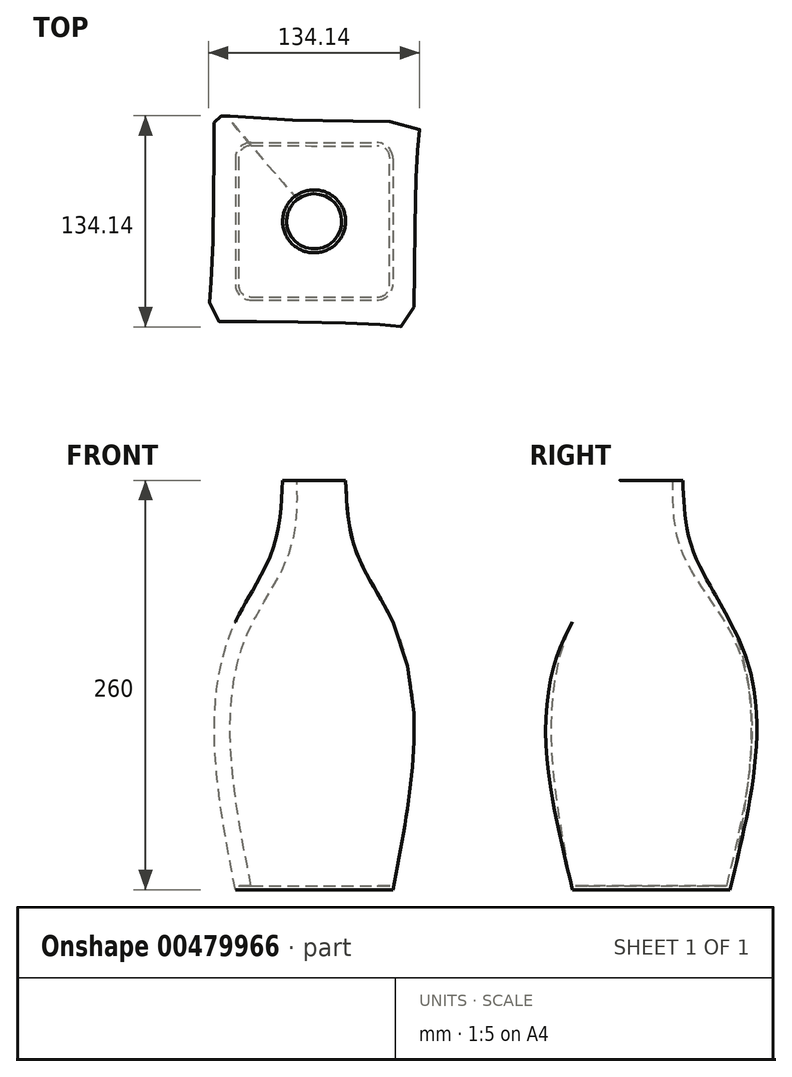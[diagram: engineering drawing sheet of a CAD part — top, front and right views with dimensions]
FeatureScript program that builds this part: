
annotation { "Feature Type Name" : "Feature", "Feature Type Description" : "" }
export const myFeature = defineFeature(function(context is Context, id is Id, definition is map)
    precondition{}
    {
        {
            var Q0;
            Q0=qCreatedBy(makeId("Top.planeOp"),FACE);
            var sketch = newSketch(context, id + "F0", { "sketchPlane" : qUnion([Q0])});
            skLineSegment(sketch, "E0.bottom", {"start": v(10, 0) * mm, "end": v(90, 0) * mm});
            skLineSegment(sketch, "E0.top", {"start": v(10, -100) * mm, "end": v(90, -100) * mm});
            skLineSegment(sketch, "E0.left", {"start": v(0, -10) * mm, "end": v(0, -90) * mm});
            skLineSegment(sketch, "E0.right", {"start": v(100, -10) * mm, "end": v(100, -90) * mm});
            skPoint(sketch, "E1.visualSharp", {"position": v(0, 0) * mm});
            skArc(sketch, "E1.filletArc", {"start": v(10, 0) * mm, "mid": v(2.93, -2.93) * mm, "end": v(0, -10) * mm});
            skPoint(sketch, "E2.visualSharp", {"position": v(100, 0) * mm});
            skArc(sketch, "E2.filletArc", {"start": v(100, -10) * mm, "mid": v(97.07, -2.93) * mm, "end": v(90, 0) * mm});
            skPoint(sketch, "E3.visualSharp", {"position": v(100, -100) * mm});
            skArc(sketch, "E3.filletArc", {"start": v(90, -100) * mm, "mid": v(97.07, -97.07) * mm, "end": v(100, -90) * mm});
            skPoint(sketch, "E4.visualSharp", {"position": v(0, -100) * mm});
            skArc(sketch, "E4.filletArc", {"start": v(0, -90) * mm, "mid": v(2.93, -97.07) * mm, "end": v(10, -100) * mm});
            skSolve(sketch);
        }
        {
            var Q0;
            Q0=qCreatedBy(makeId("Top.planeOp"),FACE);
            cPlane(context, id + "F1", {"entities" : qUnion([Q0]), "cplaneType" : CPlaneType.OFFSET, "offset" : 170 * mm, "width" : 150 * mm, "height" : 150 * mm});
        }
        {
            var Q0;
            Q0=qCreatedBy(id+"F1.planeOp",FACE);
            cPlane(context, id + "F2", {"entities" : qUnion([Q0]), "cplaneType" : CPlaneType.OFFSET, "offset" : 50 * mm, "width" : 150 * mm, "height" : 150 * mm});
        }
        {
            var Q0;
            Q0=qCreatedBy(id+"F2.planeOp",FACE);
            cPlane(context, id + "F3", {"entities" : qUnion([Q0]), "cplaneType" : CPlaneType.OFFSET, "offset" : 40 * mm, "width" : 150 * mm, "height" : 150 * mm});
        }
        {
            var Q0;
            Q0=qCreatedBy(id+"F1.planeOp",FACE);
            var sketch = newSketch(context, id + "F4", { "sketchPlane" : qUnion([Q0])});
            skLineSegment(sketch, "E5.bottom", {"start": v(10, 0) * mm, "end": v(90, 0) * mm});
            skLineSegment(sketch, "E5.top", {"start": v(10, -100) * mm, "end": v(90, -100) * mm});
            skLineSegment(sketch, "E5.left", {"start": v(0, -10) * mm, "end": v(0, -90) * mm});
            skLineSegment(sketch, "E5.right", {"start": v(100, -10) * mm, "end": v(100, -90) * mm});
            skPoint(sketch, "E6.visualSharp", {"position": v(100, 0) * mm});
            skArc(sketch, "E6.filletArc", {"start": v(100, -10) * mm, "mid": v(97.07, -2.93) * mm, "end": v(90, 0) * mm});
            skPoint(sketch, "E7.visualSharp", {"position": v(0, 0) * mm});
            skArc(sketch, "E7.filletArc", {"start": v(10, 0) * mm, "mid": v(2.93, -2.93) * mm, "end": v(0, -10) * mm});
            skPoint(sketch, "E8.visualSharp", {"position": v(0, -100) * mm});
            skArc(sketch, "E8.filletArc", {"start": v(0, -90) * mm, "mid": v(2.93, -97.07) * mm, "end": v(10, -100) * mm});
            skPoint(sketch, "E9.visualSharp", {"position": v(100, -100) * mm});
            skArc(sketch, "E9.filletArc", {"start": v(90, -100) * mm, "mid": v(97.07, -97.07) * mm, "end": v(100, -90) * mm});
            skSolve(sketch);
        }
        {
            var Q0;
            Q0=qCreatedBy(id+"F2.planeOp",FACE);
            var sketch = newSketch(context, id + "F5", { "sketchPlane" : qUnion([Q0])});
            skCircle(sketch, "E10", {"center": v(50, -50) * mm, "radius": 25 * mm});
            skPoint(sketch, "E10.centerSnap0", {"position": v(0, -50) * mm});
            skPoint(sketch, "E10.centerSnap1", {"position": v(50, 0) * mm});
            skSolve(sketch);
        }
        {
            var Q0;
            Q0=qCreatedBy(id+"F3.planeOp",FACE);
            var sketch = newSketch(context, id + "F6", { "sketchPlane" : qUnion([Q0])});
            skCircle(sketch, "E11", {"center": v(50, -50) * mm, "radius": 20 * mm});
            skPoint(sketch, "E11.centerSnap0", {"position": v(50, 0) * mm});
            skPoint(sketch, "E11.centerSnap1", {"position": v(0, -50) * mm});
            skSolve(sketch);
        }
        {
            var Q0;
            Q0=makeQuery(id+"F0.imprint","IMPRINT",FACE,{"disambiguationData":[TD([[makeQuery(id+"F0.imprint","IMPRINT",EDGE,{"derivedFrom":sQuery(id+"F0.wireOp",EDGE,"E0.bottom")}),-1.0]])]});
            var Q1;
            Q1=makeQuery(id+"F4.imprint","IMPRINT",FACE,{"disambiguationData":[TD([[makeQuery(id+"F4.imprint","IMPRINT",EDGE,{"derivedFrom":sQuery(id+"F4.wireOp",EDGE,"E5.bottom")}),-1.0]])]});
            var Q2;
            Q2=makeQuery(id+"F5.imprint","IMPRINT",FACE,{"disambiguationData":[TD([[makeQuery(id+"F5.imprint","IMPRINT",EDGE,{"derivedFrom":sQuery(id+"F5.wireOp",EDGE,"E10")}),1.0]])]});
            var Q3;
            Q3=makeQuery(id+"F6.imprint","IMPRINT",FACE,{"disambiguationData":[TD([[makeQuery(id+"F6.imprint","IMPRINT",EDGE,{"derivedFrom":sQuery(id+"F6.wireOp",EDGE,"E11")}),1.0]])]});
            loft(context, id + "F7", {"sheetProfilesArray" : [{ "sheetProfileEntities" : qUnion([Q0]) }, { "sheetProfileEntities" : qUnion([Q1]) }, { "sheetProfileEntities" : qUnion([Q2]) }, { "sheetProfileEntities" : qUnion([Q3]) }]});
        }
        {
            var Q0;
            Q0=makeQuery(id+"F7.opLoft","CAP_FACE",FACE,{"disambiguationData":[OSD([makeQuery(id+"F6.imprint","IMPRINT",FACE,{"disambiguationData":[TD([[makeQuery(id+"F6.imprint","IMPRINT",EDGE,{"derivedFrom":sQuery(id+"F6.wireOp",EDGE,"E11")}),1.0]])]})])],"isStart":true});
            shell(context, id + "F8", {"entities" : qUnion([Q0]), "thickness" : 2.5 * mm});
        }
    });
